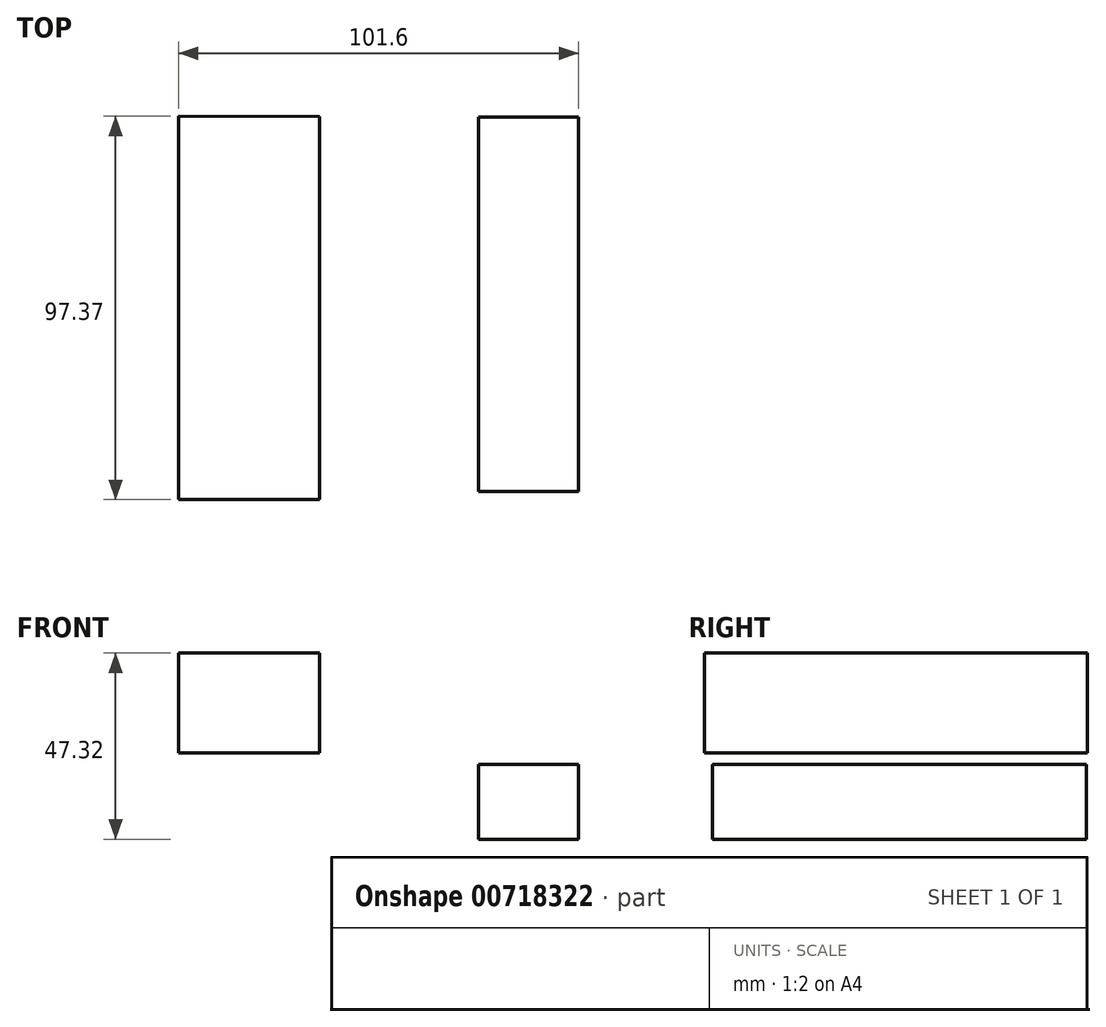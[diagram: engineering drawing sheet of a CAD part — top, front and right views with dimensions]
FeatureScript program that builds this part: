
annotation { "Feature Type Name" : "Feature", "Feature Type Description" : "" }
export const myFeature = defineFeature(function(context is Context, id is Id, definition is map)
    precondition{}
    {
        {
            var Q0;
            Q0=qCreatedBy(makeId("Top.planeOp"),FACE);
            var sketch = newSketch(context, id + "F0", { "sketchPlane" : qUnion([Q0])});
            skLineSegment(sketch, "E0", {"start": v(-76.2, 54.82) * mm, "end": v(-76.2, -42.55) * mm});
            skLineSegment(sketch, "E1", {"start": v(-76.2, -42.55) * mm, "end": v(-40.42, -42.55) * mm});
            skLineSegment(sketch, "E2", {"start": v(-40.42, -42.55) * mm, "end": v(-40.42, 54.79) * mm});
            skLineSegment(sketch, "E3", {"start": v(-40.42, 54.79) * mm, "end": v(-76.2, 54.82) * mm});
            skSolve(sketch);
        }
        {
            var Q0;
            Q0=qCreatedBy(makeId("Right.planeOp"),FACE);
            var sketch = newSketch(context, id + "F1", { "sketchPlane" : qUnion([Q0])});
            skLineSegment(sketch, "E4", {"start": v(-40.51, -2.9) * mm, "end": v(-40.51, -21.92) * mm});
            skLineSegment(sketch, "E5", {"start": v(-40.51, -21.92) * mm, "end": v(54.55, -21.92) * mm});
            skLineSegment(sketch, "E6", {"start": v(54.55, -21.92) * mm, "end": v(54.55, -2.9) * mm});
            skLineSegment(sketch, "E7", {"start": v(54.55, -2.9) * mm, "end": v(-40.51, -2.9) * mm});
            skSolve(sketch);
        }
        {
            var Q0;
            Q0 = qSketchRegion(id + "F1", true);
            extrude(context, id + "F2", {"entities" : qUnion([Q0]), "depth" : 25.4 * mm, "offsetDistance" : 25.4 * mm});
        }
        {
            var Q0;
            Q0 = qSketchRegion(id + "F0", true);
            extrude(context, id + "F3", {"entities" : qUnion([Q0]), "depth" : 25.4 * mm, "offsetDistance" : 25.4 * mm});
        }
    });
